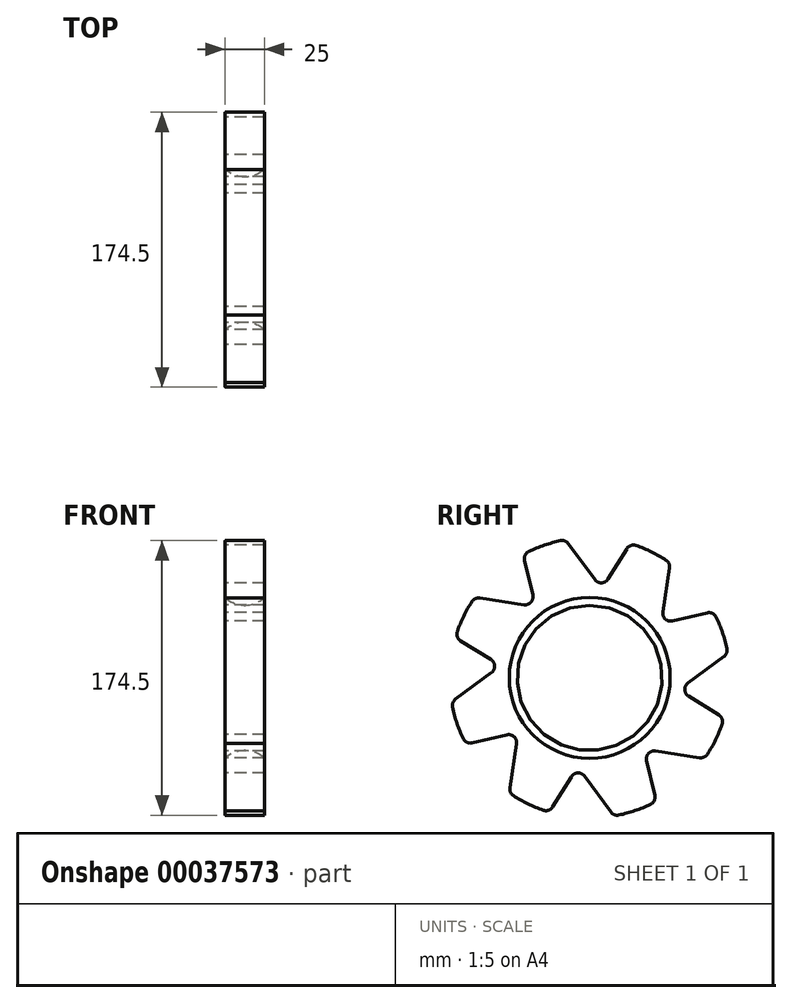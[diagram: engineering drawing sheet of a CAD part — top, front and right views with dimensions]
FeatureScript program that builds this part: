
annotation { "Feature Type Name" : "Feature", "Feature Type Description" : "" }
export const myFeature = defineFeature(function(context is Context, id is Id, definition is map)
    precondition{}
    {
        {
            var Q0;
            Q0=qCreatedBy(makeId("Top.planeOp"),FACE);
            var sketch = newSketch(context, id + "F0", { "sketchPlane" : qUnion([Q0])});
            skLineSegment(sketch, "E0", {"start": v(-134.1, 0) * mm, "end": v(143.87, 0) * mm, "construction": true});
            skArc(sketch, "E1", {"start": v(-12.5, 51.1) * mm, "mid": v(0, 46.14) * mm, "end": v(12.5, 51.1) * mm});
            skPoint(sketch, "E2.visualSharp", {"position": v(-12.5, 89.1) * mm});
            skPoint(sketch, "E3.visualSharp", {"position": v(12.5, 89.1) * mm});
            skLineSegment(sketch, "E4", {"start": v(-12.5, 89.1) * mm, "end": v(-12.5, 51.1) * mm});
            skLineSegment(sketch, "E5", {"start": v(12.5, 51.1) * mm, "end": v(12.5, 89.1) * mm});
            skLineSegment(sketch, "E6", {"start": v(-12.5, 89.1) * mm, "end": v(12.5, 89.1) * mm});
            skSolve(sketch);
        }
        {
            var Q0;
            Q0=makeQuery(id+"F0.imprint","IMPRINT",FACE,{"disambiguationData":[TD([[makeQuery(id+"F0.imprint","IMPRINT",EDGE,{"derivedFrom":sQuery(id+"F0.wireOp",EDGE,"925d6d46-2ef4-4108-8e87-6c8beadc732d.left")}),1.0]])]});
            var Q1;
            Q1=makeQuery(id+"F0.imprint","IMPRINT",FACE,{"disambiguationData":[TD([[makeQuery(id+"F0.imprint","IMPRINT",EDGE,{"derivedFrom":sQuery(id+"F0.wireOp",EDGE,"E1")}),1.0]])]});
            var Q2;
            Q2=sQuery(id+"F0.wireOp",EDGE,"E0");
            revolve(context, id + "F1", {"entities" : qUnion([Q0, Q1]), "axis" : qUnion([Q2]), "revolveType" : RevolveType.FULL});
        }
        {
            var Q0;
            Q0=qCreatedBy(makeId("Right.planeOp"),FACE);
            cPlane(context, id + "F2", {"entities" : qUnion([Q0]), "cplaneType" : CPlaneType.OFFSET, "offset" : 15 * mm, "width" : 150 * mm, "height" : 150 * mm});
        }
        {
            var Q0;
            Q0=qCreatedBy(id+"F2.planeOp",FACE);
            var sketch = newSketch(context, id + "F3", { "sketchPlane" : qUnion([Q0])});
            skLineSegment(sketch, "E7", {"start": v(-88.9, 27.83) * mm, "end": v(-56.46, 7.7) * mm});
            skLineSegment(sketch, "E8", {"start": v(-56.46, 7.7) * mm, "end": v(-93.65, -19.7) * mm});
            skLineSegment(sketch, "E9", {"start": v(-93.65, -19.7) * mm, "end": v(-88.9, 27.83) * mm});
            skLineSegment(sketch, "E10.1.0", {"start": v(-52.29, -80.16) * mm, "end": v(-82.54, -43.18) * mm});
            skLineSegment(sketch, "E10.1.1", {"start": v(-82.54, -43.18) * mm, "end": v(-45.36, -34.48) * mm});
            skLineSegment(sketch, "E10.1.2", {"start": v(-45.36, -34.48) * mm, "end": v(-52.29, -80.16) * mm});
            skLineSegment(sketch, "E10.2.0", {"start": v(19.7, -93.65) * mm, "end": v(-27.83, -88.9) * mm});
            skLineSegment(sketch, "E10.2.1", {"start": v(-27.83, -88.9) * mm, "end": v(-7.7, -56.46) * mm});
            skLineSegment(sketch, "E10.2.2", {"start": v(-7.7, -56.46) * mm, "end": v(19.7, -93.65) * mm});
            skLineSegment(sketch, "E10.3.0", {"start": v(80.16, -52.29) * mm, "end": v(43.18, -82.54) * mm});
            skLineSegment(sketch, "E10.3.1", {"start": v(43.18, -82.54) * mm, "end": v(34.48, -45.36) * mm});
            skLineSegment(sketch, "E10.3.2", {"start": v(34.48, -45.36) * mm, "end": v(80.16, -52.29) * mm});
            skLineSegment(sketch, "E10.4.0", {"start": v(93.65, 19.7) * mm, "end": v(88.9, -27.83) * mm});
            skLineSegment(sketch, "E10.4.1", {"start": v(88.9, -27.83) * mm, "end": v(56.46, -7.7) * mm});
            skLineSegment(sketch, "E10.4.2", {"start": v(56.46, -7.7) * mm, "end": v(93.65, 19.7) * mm});
            skLineSegment(sketch, "E10.5.0", {"start": v(52.29, 80.16) * mm, "end": v(82.54, 43.18) * mm});
            skLineSegment(sketch, "E10.5.1", {"start": v(82.54, 43.18) * mm, "end": v(45.36, 34.48) * mm});
            skLineSegment(sketch, "E10.5.2", {"start": v(45.36, 34.48) * mm, "end": v(52.29, 80.16) * mm});
            skLineSegment(sketch, "E10.6.0", {"start": v(-19.7, 93.65) * mm, "end": v(27.83, 88.9) * mm});
            skLineSegment(sketch, "E10.6.1", {"start": v(27.83, 88.9) * mm, "end": v(7.7, 56.46) * mm});
            skLineSegment(sketch, "E10.6.2", {"start": v(7.7, 56.46) * mm, "end": v(-19.7, 93.65) * mm});
            skLineSegment(sketch, "E10.7.0", {"start": v(-80.16, 52.29) * mm, "end": v(-43.18, 82.54) * mm});
            skLineSegment(sketch, "E10.7.1", {"start": v(-43.18, 82.54) * mm, "end": v(-34.48, 45.36) * mm});
            skLineSegment(sketch, "E10.7.2", {"start": v(-34.48, 45.36) * mm, "end": v(-80.16, 52.29) * mm});
            skPoint(sketch, "E10.center", {"position": v(0, 0) * mm});
            skLineSegment(sketch, "E11", {"start": v(-48.07, -71.65) * mm, "end": v(-27.54, -81.36) * mm, "construction": true});
            skLineSegment(sketch, "E12.1.0", {"start": v(16.67, -84.66) * mm, "end": v(38.06, -77) * mm, "construction": true});
            skLineSegment(sketch, "E12.2.0", {"start": v(71.65, -48.07) * mm, "end": v(81.36, -27.54) * mm, "construction": true});
            skLineSegment(sketch, "E12.3.0", {"start": v(84.66, 16.67) * mm, "end": v(77, 38.06) * mm, "construction": true});
            skLineSegment(sketch, "E12.4.0", {"start": v(48.07, 71.65) * mm, "end": v(27.54, 81.36) * mm, "construction": true});
            skLineSegment(sketch, "E12.5.0", {"start": v(-16.67, 84.66) * mm, "end": v(-38.06, 77) * mm, "construction": true});
            skLineSegment(sketch, "E12.6.0", {"start": v(-71.65, 48.07) * mm, "end": v(-81.36, 27.54) * mm, "construction": true});
            skLineSegment(sketch, "E12.7.0", {"start": v(-84.66, -16.67) * mm, "end": v(-77, -38.06) * mm, "construction": true});
            skSolve(sketch);
        }
        {
            var Q0;
            Q0=makeQuery(id+"F3.imprint","IMPRINT",FACE,{"disambiguationData":[TD([[makeQuery(id+"F3.imprint","IMPRINT",EDGE,{"derivedFrom":sQuery(id+"F3.wireOp",EDGE,"E10.3.0")}),-1.0]])]});
            var Q1;
            Q1=makeQuery(id+"F3.imprint","IMPRINT",FACE,{"disambiguationData":[TD([[makeQuery(id+"F3.imprint","IMPRINT",EDGE,{"derivedFrom":sQuery(id+"F3.wireOp",EDGE,"E10.2.0")}),-1.0]])]});
            var Q2;
            Q2=makeQuery(id+"F3.imprint","IMPRINT",FACE,{"disambiguationData":[TD([[makeQuery(id+"F3.imprint","IMPRINT",EDGE,{"derivedFrom":sQuery(id+"F3.wireOp",EDGE,"E10.1.0")}),-1.0]])]});
            var Q3;
            Q3=makeQuery(id+"F3.imprint","IMPRINT",FACE,{"disambiguationData":[TD([[makeQuery(id+"F3.imprint","IMPRINT",EDGE,{"derivedFrom":sQuery(id+"F3.wireOp",EDGE,"E7")}),-1.0]])]});
            var Q4;
            Q4=makeQuery(id+"F3.imprint","IMPRINT",FACE,{"disambiguationData":[TD([[makeQuery(id+"F3.imprint","IMPRINT",EDGE,{"derivedFrom":sQuery(id+"F3.wireOp",EDGE,"E10.7.0")}),-1.0]])]});
            var Q5;
            Q5=makeQuery(id+"F3.imprint","IMPRINT",FACE,{"disambiguationData":[TD([[makeQuery(id+"F3.imprint","IMPRINT",EDGE,{"derivedFrom":sQuery(id+"F3.wireOp",EDGE,"E10.6.0")}),-1.0]])]});
            var Q6;
            Q6=makeQuery(id+"F3.imprint","IMPRINT",FACE,{"disambiguationData":[TD([[makeQuery(id+"F3.imprint","IMPRINT",EDGE,{"derivedFrom":sQuery(id+"F3.wireOp",EDGE,"E10.5.0")}),-1.0]])]});
            var Q7;
            Q7=makeQuery(id+"F3.imprint","IMPRINT",FACE,{"disambiguationData":[TD([[makeQuery(id+"F3.imprint","IMPRINT",EDGE,{"derivedFrom":sQuery(id+"F3.wireOp",EDGE,"E10.4.0")}),-1.0]])]});
            extrude(context, id + "F4", {"entities" : qUnion([Q0, Q1, Q2, Q3, Q4, Q5, Q6, Q7]), "operationType" : NewBodyOperationType.REMOVE, "oppositeDirection" : true, "depth" : 60 * mm});
        }
        {
            var Q0;
            Q0=makeQuery(id+"F4.boolean.opBoolean","INTERSECT",EDGE,{"derivedFrom":[makeQuery(id+"F1.opRevolve","SWEPT_FACE",FACE,{"disambiguationData":[OSD([sQuery(id+"F0.wireOp",EDGE,"E6")])]}),makeQuery(id+"F4.opExtrude","SWEPT_FACE",FACE,{"disambiguationData":[OSD([sQuery(id+"F3.wireOp",EDGE,"E10.4.2")])]})]});
            var Q1;
            Q1=makeQuery(id+"F4.boolean.opBoolean","INTERSECT",EDGE,{"derivedFrom":[makeQuery(id+"F1.opRevolve","SWEPT_FACE",FACE,{"disambiguationData":[OSD([sQuery(id+"F0.wireOp",EDGE,"E6")])]}),makeQuery(id+"F4.opExtrude","SWEPT_FACE",FACE,{"disambiguationData":[OSD([sQuery(id+"F3.wireOp",EDGE,"E10.4.1")])]})]});
            var Q2;
            Q2=makeQuery(id+"F4.boolean.opBoolean","INTERSECT",EDGE,{"derivedFrom":[makeQuery(id+"F1.opRevolve","SWEPT_FACE",FACE,{"disambiguationData":[OSD([sQuery(id+"F0.wireOp",EDGE,"E6")])]}),makeQuery(id+"F4.opExtrude","SWEPT_FACE",FACE,{"disambiguationData":[OSD([sQuery(id+"F3.wireOp",EDGE,"E10.3.2")])]})]});
            var Q3;
            Q3=makeQuery(id+"F4.boolean.opBoolean","INTERSECT",EDGE,{"derivedFrom":[makeQuery(id+"F1.opRevolve","SWEPT_FACE",FACE,{"disambiguationData":[OSD([sQuery(id+"F0.wireOp",EDGE,"E6")])]}),makeQuery(id+"F4.opExtrude","SWEPT_FACE",FACE,{"disambiguationData":[OSD([sQuery(id+"F3.wireOp",EDGE,"E10.5.1")])]})]});
            var Q4;
            Q4=makeQuery(id+"F4.boolean.opBoolean","INTERSECT",EDGE,{"derivedFrom":[makeQuery(id+"F1.opRevolve","SWEPT_FACE",FACE,{"disambiguationData":[OSD([sQuery(id+"F0.wireOp",EDGE,"E6")])]}),makeQuery(id+"F4.opExtrude","SWEPT_FACE",FACE,{"disambiguationData":[OSD([sQuery(id+"F3.wireOp",EDGE,"E10.5.2")])]})]});
            var Q5;
            Q5=makeQuery(id+"F4.boolean.opBoolean","INTERSECT",EDGE,{"derivedFrom":[makeQuery(id+"F1.opRevolve","SWEPT_FACE",FACE,{"disambiguationData":[OSD([sQuery(id+"F0.wireOp",EDGE,"E6")])]}),makeQuery(id+"F4.opExtrude","SWEPT_FACE",FACE,{"disambiguationData":[OSD([sQuery(id+"F3.wireOp",EDGE,"E10.3.1")])]})]});
            var Q6;
            Q6=makeQuery(id+"F4.boolean.opBoolean","INTERSECT",EDGE,{"derivedFrom":[makeQuery(id+"F1.opRevolve","SWEPT_FACE",FACE,{"disambiguationData":[OSD([sQuery(id+"F0.wireOp",EDGE,"E6")])]}),makeQuery(id+"F4.opExtrude","SWEPT_FACE",FACE,{"disambiguationData":[OSD([sQuery(id+"F3.wireOp",EDGE,"E10.2.2")])]})]});
            var Q7;
            Q7=makeQuery(id+"F4.boolean.opBoolean","COPY",EDGE,{"derivedFrom":makeQuery(id+"F4.opExtrude","SWEPT_EDGE",EDGE,{"disambiguationData":[OSD([sQuery(id+"F3.wireOp",EDGE,"E10.3.1"),sQuery(id+"F3.wireOp",EDGE,"E10.3.2")])]})});
            var Q8;
            Q8=makeQuery(id+"F4.boolean.opBoolean","COPY",EDGE,{"derivedFrom":makeQuery(id+"F4.opExtrude","SWEPT_EDGE",EDGE,{"disambiguationData":[OSD([sQuery(id+"F3.wireOp",EDGE,"E10.4.1"),sQuery(id+"F3.wireOp",EDGE,"E10.4.2")])]})});
            var Q9;
            Q9=makeQuery(id+"F4.boolean.opBoolean","COPY",EDGE,{"derivedFrom":makeQuery(id+"F4.opExtrude","SWEPT_EDGE",EDGE,{"disambiguationData":[OSD([sQuery(id+"F3.wireOp",EDGE,"E10.5.1"),sQuery(id+"F3.wireOp",EDGE,"E10.5.2")])]})});
            var Q10;
            Q10=makeQuery(id+"F4.boolean.opBoolean","INTERSECT",EDGE,{"derivedFrom":[makeQuery(id+"F1.opRevolve","SWEPT_FACE",FACE,{"disambiguationData":[OSD([sQuery(id+"F0.wireOp",EDGE,"E6")])]}),makeQuery(id+"F4.opExtrude","SWEPT_FACE",FACE,{"disambiguationData":[OSD([sQuery(id+"F3.wireOp",EDGE,"E10.6.1")])]})]});
            var Q11;
            Q11=makeQuery(id+"F4.boolean.opBoolean","COPY",EDGE,{"derivedFrom":makeQuery(id+"F4.opExtrude","SWEPT_EDGE",EDGE,{"disambiguationData":[OSD([sQuery(id+"F3.wireOp",EDGE,"E10.6.1"),sQuery(id+"F3.wireOp",EDGE,"E10.6.2")])]})});
            var Q12;
            Q12=makeQuery(id+"F4.boolean.opBoolean","INTERSECT",EDGE,{"derivedFrom":[makeQuery(id+"F1.opRevolve","SWEPT_FACE",FACE,{"disambiguationData":[OSD([sQuery(id+"F0.wireOp",EDGE,"E6")])]}),makeQuery(id+"F4.opExtrude","SWEPT_FACE",FACE,{"disambiguationData":[OSD([sQuery(id+"F3.wireOp",EDGE,"E10.6.2")])]})]});
            var Q13;
            Q13=makeQuery(id+"F4.boolean.opBoolean","INTERSECT",EDGE,{"derivedFrom":[makeQuery(id+"F1.opRevolve","SWEPT_FACE",FACE,{"disambiguationData":[OSD([sQuery(id+"F0.wireOp",EDGE,"E6")])]}),makeQuery(id+"F4.opExtrude","SWEPT_FACE",FACE,{"disambiguationData":[OSD([sQuery(id+"F3.wireOp",EDGE,"E10.7.1")])]})]});
            var Q14;
            Q14=makeQuery(id+"F4.boolean.opBoolean","COPY",EDGE,{"derivedFrom":makeQuery(id+"F4.opExtrude","SWEPT_EDGE",EDGE,{"disambiguationData":[OSD([sQuery(id+"F3.wireOp",EDGE,"E10.7.1"),sQuery(id+"F3.wireOp",EDGE,"E10.7.2")])]})});
            var Q15;
            Q15=makeQuery(id+"F4.boolean.opBoolean","INTERSECT",EDGE,{"derivedFrom":[makeQuery(id+"F1.opRevolve","SWEPT_FACE",FACE,{"disambiguationData":[OSD([sQuery(id+"F0.wireOp",EDGE,"E6")])]}),makeQuery(id+"F4.opExtrude","SWEPT_FACE",FACE,{"disambiguationData":[OSD([sQuery(id+"F3.wireOp",EDGE,"E10.7.2")])]})]});
            var Q16;
            Q16=makeQuery(id+"F4.boolean.opBoolean","INTERSECT",EDGE,{"derivedFrom":[makeQuery(id+"F1.opRevolve","SWEPT_FACE",FACE,{"disambiguationData":[OSD([sQuery(id+"F0.wireOp",EDGE,"E6")])]}),makeQuery(id+"F4.opExtrude","SWEPT_FACE",FACE,{"disambiguationData":[OSD([sQuery(id+"F3.wireOp",EDGE,"E7")])]})]});
            var Q17;
            Q17=makeQuery(id+"F4.boolean.opBoolean","COPY",EDGE,{"derivedFrom":makeQuery(id+"F4.opExtrude","SWEPT_EDGE",EDGE,{"disambiguationData":[OSD([sQuery(id+"F3.wireOp",EDGE,"E7"),sQuery(id+"F3.wireOp",EDGE,"E8")])]})});
            var Q18;
            Q18=makeQuery(id+"F4.boolean.opBoolean","INTERSECT",EDGE,{"derivedFrom":[makeQuery(id+"F1.opRevolve","SWEPT_FACE",FACE,{"disambiguationData":[OSD([sQuery(id+"F0.wireOp",EDGE,"E6")])]}),makeQuery(id+"F4.opExtrude","SWEPT_FACE",FACE,{"disambiguationData":[OSD([sQuery(id+"F3.wireOp",EDGE,"E8")])]})]});
            var Q19;
            Q19=makeQuery(id+"F4.boolean.opBoolean","INTERSECT",EDGE,{"derivedFrom":[makeQuery(id+"F1.opRevolve","SWEPT_FACE",FACE,{"disambiguationData":[OSD([sQuery(id+"F0.wireOp",EDGE,"E6")])]}),makeQuery(id+"F4.opExtrude","SWEPT_FACE",FACE,{"disambiguationData":[OSD([sQuery(id+"F3.wireOp",EDGE,"E10.1.1")])]})]});
            var Q20;
            Q20=makeQuery(id+"F4.boolean.opBoolean","COPY",EDGE,{"derivedFrom":makeQuery(id+"F4.opExtrude","SWEPT_EDGE",EDGE,{"disambiguationData":[OSD([sQuery(id+"F3.wireOp",EDGE,"E10.1.1"),sQuery(id+"F3.wireOp",EDGE,"E10.1.2")])]})});
            var Q21;
            Q21=makeQuery(id+"F4.boolean.opBoolean","INTERSECT",EDGE,{"derivedFrom":[makeQuery(id+"F1.opRevolve","SWEPT_FACE",FACE,{"disambiguationData":[OSD([sQuery(id+"F0.wireOp",EDGE,"E6")])]}),makeQuery(id+"F4.opExtrude","SWEPT_FACE",FACE,{"disambiguationData":[OSD([sQuery(id+"F3.wireOp",EDGE,"E10.1.2")])]})]});
            var Q22;
            Q22=makeQuery(id+"F4.boolean.opBoolean","INTERSECT",EDGE,{"derivedFrom":[makeQuery(id+"F1.opRevolve","SWEPT_FACE",FACE,{"disambiguationData":[OSD([sQuery(id+"F0.wireOp",EDGE,"E6")])]}),makeQuery(id+"F4.opExtrude","SWEPT_FACE",FACE,{"disambiguationData":[OSD([sQuery(id+"F3.wireOp",EDGE,"E10.2.1")])]})]});
            var Q23;
            Q23=makeQuery(id+"F4.boolean.opBoolean","COPY",EDGE,{"derivedFrom":makeQuery(id+"F4.opExtrude","SWEPT_EDGE",EDGE,{"disambiguationData":[OSD([sQuery(id+"F3.wireOp",EDGE,"E10.2.1"),sQuery(id+"F3.wireOp",EDGE,"E10.2.2")])]})});
            fillet(context, id + "F5", {"entities" : qUnion([Q0, Q1, Q2, Q3, Q4, Q5, Q6, Q7, Q8, Q9, Q10, Q11, Q12, Q13, Q14, Q15, Q16, Q17, Q18, Q19, Q20, Q21, Q22, Q23]), "radius" : 5 * mm, "tangentPropagation" : true, "allowEdgeOverflow" : false});
        }
    });
